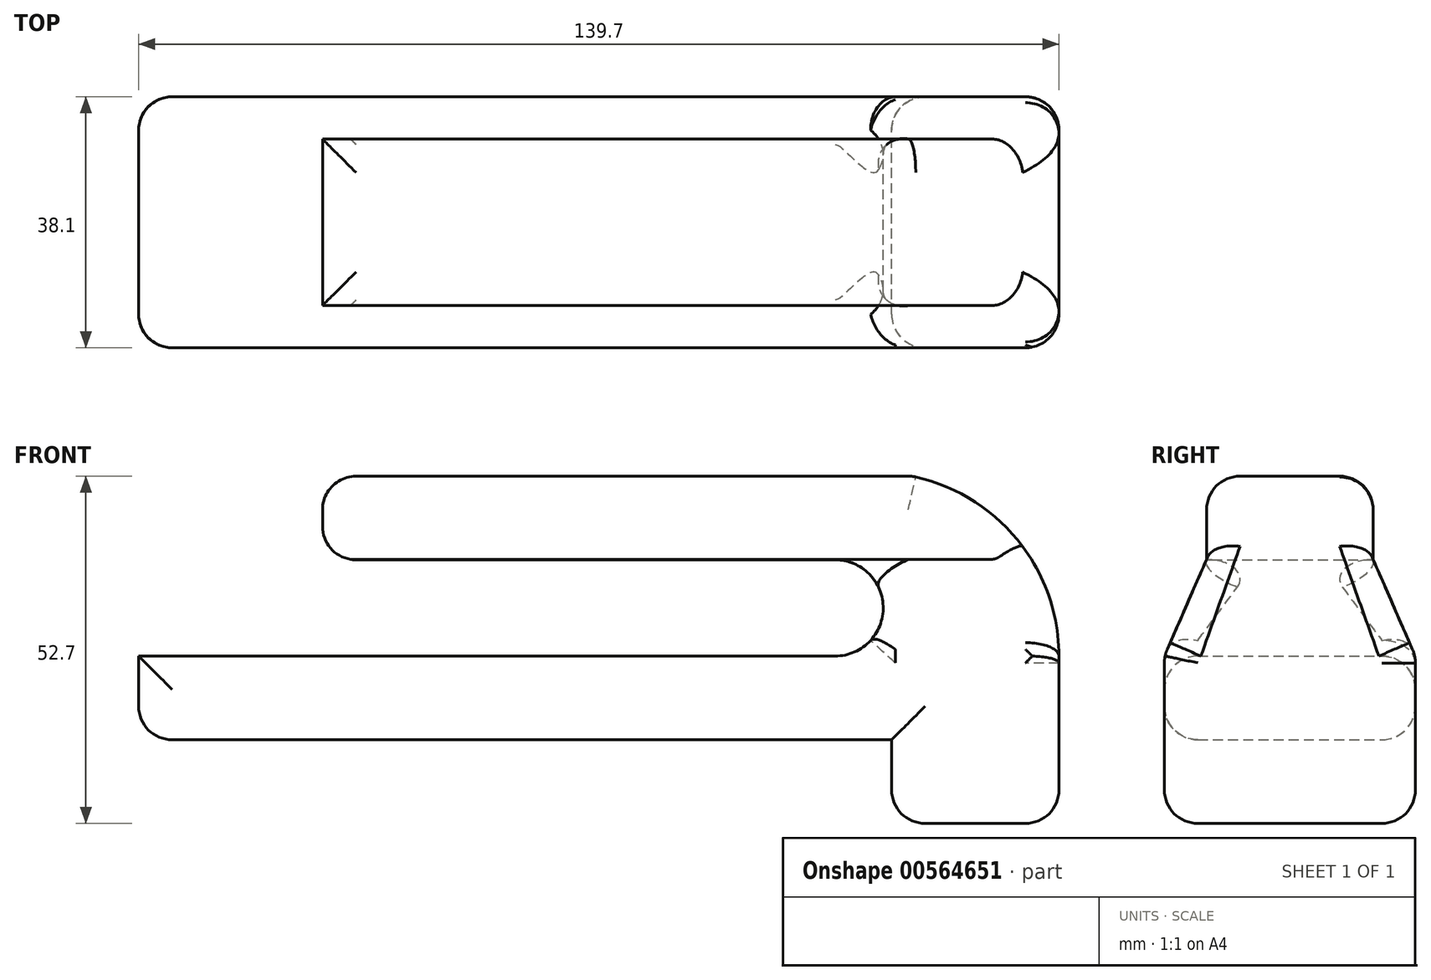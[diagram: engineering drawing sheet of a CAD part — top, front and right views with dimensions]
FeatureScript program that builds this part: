
annotation { "Feature Type Name" : "Feature", "Feature Type Description" : "" }
export const myFeature = defineFeature(function(context is Context, id is Id, definition is map)
    precondition{}
    {
        {
            var Q0;
            Q0=qCreatedBy(makeId("Front.planeOp"),FACE);
            var sketch = newSketch(context, id + "F0", { "sketchPlane" : qUnion([Q0])});
            skLineSegment(sketch, "E0.bottom", {"start": v(67.16, 0) * mm, "end": v(-72.54, 0) * mm});
            skLineSegment(sketch, "E0.left", {"start": v(67.16, 0) * mm, "end": v(67.16, 12.7) * mm});
            skLineSegment(sketch, "E0.right", {"start": v(-72.54, 0) * mm, "end": v(-72.54, 12.7) * mm});
            skLineSegment(sketch, "E1", {"start": v(-44.62, 27.3) * mm, "end": v(-44.62, 40) * mm});
            skLineSegment(sketch, "E2", {"start": v(-44.62, 40) * mm, "end": v(44.84, 40) * mm});
            skArc(sketch, "E3", {"start": v(67.16, 12.7) * mm, "mid": v(60.87, 30.33) * mm, "end": v(44.84, 40) * mm});
            skLineSegment(sketch, "E4", {"start": v(73.54, 0) * mm, "end": v(73.54, 49.57) * mm});
            skLineSegment(sketch, "E5", {"start": v(-44.62, 27.3) * mm, "end": v(33.18, 27.3) * mm});
            skArc(sketch, "E6", {"start": v(33.18, 12.7) * mm, "mid": v(40.48, 20) * mm, "end": v(33.18, 27.3) * mm});
            skLineSegment(sketch, "E7", {"start": v(-72.54, 12.7) * mm, "end": v(33.18, 12.7) * mm});
            skLineSegment(sketch, "E8.bottom", {"start": v(67.16, 0) * mm, "end": v(41.76, 0) * mm});
            skLineSegment(sketch, "E8.top", {"start": v(67.16, -12.7) * mm, "end": v(41.76, -12.7) * mm});
            skLineSegment(sketch, "E8.left", {"start": v(67.16, 0) * mm, "end": v(67.16, -12.7) * mm});
            skLineSegment(sketch, "E8.right", {"start": v(41.76, 0) * mm, "end": v(41.76, -12.7) * mm});
            skSolve(sketch);
        }
        {
            var Q0;
            Q0=qSketchRegion(id+"F0",true);
            extrude(context, id + "F1", {"entities" : qUnion([Q0]), "depth" : 38.1 * mm, "offsetDistance" : 25.4 * mm});
        }
        {
            var Q0;
            Q0=qCreatedBy(makeId("Right.planeOp"),FACE);
            var sketch = newSketch(context, id + "F2", { "sketchPlane" : qUnion([Q0])});
            skLineSegment(sketch, "E9", {"start": v(0, 12.7) * mm, "end": v(0, 40.1) * mm});
            skLineSegment(sketch, "E10", {"start": v(0, 12.7) * mm, "end": v(-6.42, 27.37) * mm});
            skLineSegment(sketch, "E11", {"start": v(-31.69, 27.37) * mm, "end": v(-38.1, 12.7) * mm});
            skLineSegment(sketch, "E12", {"start": v(-31.69, 27.37) * mm, "end": v(-31.69, 45.15) * mm});
            skLineSegment(sketch, "E13", {"start": v(-31.69, 45.15) * mm, "end": v(-38.1, 45.15) * mm});
            skLineSegment(sketch, "E14", {"start": v(-38.1, 45.15) * mm, "end": v(-38.1, 12.7) * mm});
            skLineSegment(sketch, "E15", {"start": v(-6.42, 27.37) * mm, "end": v(-6.42, 45.15) * mm});
            skLineSegment(sketch, "E16", {"start": v(0, 12.7) * mm, "end": v(0, 45.15) * mm});
            skLineSegment(sketch, "E17", {"start": v(0, 45.15) * mm, "end": v(-6.42, 45.15) * mm});
            skSolve(sketch);
        }
        {
            var Q0;
            Q0=qSketchRegion(id+"F2",true);
            extrude(context, id + "F3", {"entities" : qUnion([Q0]), "operationType" : NewBodyOperationType.REMOVE, "oppositeDirection" : true, "depth" : -127 * mm, "offsetDistance" : 25.4 * mm});
        }
        {
            var Q0;
            Q0 = qSketchRegion(id + "F2", true);
            extrude(context, id + "F4", {"entities" : qUnion([Q0]), "operationType" : NewBodyOperationType.REMOVE, "depth" : -76.2 * mm, "offsetDistance" : 25.4 * mm});
        }
        {
            var Q0;
            Q0=makeQuery(id+"F4.boolean.opBoolean","INTERSECT",EDGE,{"derivedFrom":[makeQuery(id+"F1.opExtrude","SWEPT_FACE",FACE,{"disambiguationData":[OSD([sQuery(id+"F0.wireOp",EDGE,"E2")])]}),makeQuery(id+"F4.opExtrude","SWEPT_FACE",FACE,{"disambiguationData":[OSD([sQuery(id+"F2.wireOp",EDGE,"E12")])]})]});
            var Q1;
            Q1=makeQuery(id+"F4.boolean.opBoolean","INTERSECT",EDGE,{"derivedFrom":[makeQuery(id+"F1.opExtrude","SWEPT_FACE",FACE,{"disambiguationData":[OSD([sQuery(id+"F0.wireOp",EDGE,"E5")])]}),makeQuery(id+"F4.opExtrude","SWEPT_FACE",FACE,{"disambiguationData":[OSD([sQuery(id+"F2.wireOp",EDGE,"E11")])]})]});
            var Q2;
            Q2=makeQuery(id+"F3.boolean.opBoolean","INTERSECT",EDGE,{"derivedFrom":[makeQuery(id+"F1.opExtrude","SWEPT_FACE",FACE,{"disambiguationData":[OSD([sQuery(id+"F0.wireOp",EDGE,"E3")])]}),makeQuery(id+"F3.opExtrude","SWEPT_FACE",FACE,{"disambiguationData":[OSD([sQuery(id+"F2.wireOp",EDGE,"E12")])]})]});
            var Q3;
            Q3=makeQuery(id+"F3.boolean.opBoolean","INTERSECT",EDGE,{"derivedFrom":[makeQuery(id+"F1.opExtrude","SWEPT_FACE",FACE,{"disambiguationData":[OSD([sQuery(id+"F0.wireOp",EDGE,"E6")])]}),makeQuery(id+"F3.opExtrude","SWEPT_FACE",FACE,{"disambiguationData":[OSD([sQuery(id+"F2.wireOp",EDGE,"E11")])]})]});
            var Q4;
            {var subQ0=sQuery(id+"F0.wireOp",EDGE,"E7");var subQ1=sQuery(id+"F0.wireOp",EDGE,"E6");Q4=makeQuery(id+"F4.boolean.opBoolean","SPLIT",EDGE,{"disambiguationData":[TD([makeQuery(id+"F1.opExtrude","SWEPT_FACE",FACE,{"disambiguationData":[OSD([subQ1])]})])],"derivedFrom":makeQuery(id+"F1.opExtrude","CAP_EDGE",EDGE,{"disambiguationData":[OSD([subQ0])],"isStart":false})});}
            var Q5;
            {var subQ0=sQuery(id+"F0.wireOp",EDGE,"E7");var subQ1=sQuery(id+"F0.wireOp",EDGE,"E0.right");Q5=makeQuery(id+"F4.boolean.opBoolean","SPLIT",EDGE,{"disambiguationData":[TD([makeQuery(id+"F1.opExtrude","SWEPT_FACE",FACE,{"disambiguationData":[OSD([subQ1])]})])],"derivedFrom":makeQuery(id+"F1.opExtrude","CAP_EDGE",EDGE,{"disambiguationData":[OSD([subQ0])],"isStart":false})});}
            var Q6;
            Q6=makeQuery(id+"F1.opExtrude","CAP_EDGE",EDGE,{"disambiguationData":[OSD([sQuery(id+"F0.wireOp",EDGE,"E0.right")])],"isStart":false});
            var Q7;
            {var subQ0=sQuery(id+"F0.wireOp",EDGE,"E3");var subQ1=sQuery(id+"F0.wireOp",EDGE,"E0.right");var subQ2=sQuery(id+"F0.wireOp",EDGE,"E8.left");var subQ3=sQuery(id+"F0.wireOp",EDGE,"E0.left");var subQ4=sQuery(id+"F0.wireOp",EDGE,"E0.bottom");var subQ5=sQuery(id+"F0.wireOp",EDGE,"E8.top");var subQ6=sQuery(id+"F0.wireOp",EDGE,"E6");var subQ7=sQuery(id+"F0.wireOp",EDGE,"E7");var subQ8=sQuery(id+"F0.wireOp",EDGE,"E8.right");Q7=makeQuery(id+"F3.boolean.opBoolean","SPLIT",FACE,{"disambiguationData":[TD([makeQuery(id+"F1.opExtrude","SWEPT_FACE",FACE,{"disambiguationData":[OSD([subQ4])]})])],"derivedFrom":makeQuery(id+"F1.opExtrude","CAP_FACE",FACE,{"disambiguationData":[OSD([subQ4,subQ3,subQ1,sQuery(id+"F0.wireOp",EDGE,"E1"),sQuery(id+"F0.wireOp",EDGE,"E2"),subQ0,sQuery(id+"F0.wireOp",EDGE,"E5"),subQ6,subQ7,subQ5,subQ2,subQ8])],"isStart":false})});}
            var Q8;
            Q8=makeQuery(id+"F1.opExtrude","CAP_EDGE",EDGE,{"disambiguationData":[OSD([sQuery(id+"F0.wireOp",EDGE,"E8.right")])],"isStart":false});
            var Q9;
            Q9=makeQuery(id+"F1.opExtrude","CAP_EDGE",EDGE,{"disambiguationData":[OSD([sQuery(id+"F0.wireOp",EDGE,"E8.top")])],"isStart":false});
            var Q10;
            Q10=makeQuery(id+"F1.opExtrude","CAP_EDGE",EDGE,{"disambiguationData":[OSD([sQuery(id+"F0.wireOp",EDGE,"E0.left"),sQuery(id+"F0.wireOp",EDGE,"E8.left")])],"isStart":false});
            var Q11;
            Q11=makeQuery(id+"F1.opExtrude","CAP_EDGE",EDGE,{"disambiguationData":[OSD([sQuery(id+"F0.wireOp",EDGE,"E0.bottom")])],"isStart":false});
            var Q12;
            Q12=makeQuery(id+"F1.opExtrude","SWEPT_EDGE",EDGE,{"disambiguationData":[OSD([sQuery(id+"F0.wireOp",EDGE,"E1"),sQuery(id+"F0.wireOp",EDGE,"E2")])]});
            var Q13;
            Q13=makeQuery(id+"F1.opExtrude","SWEPT_EDGE",EDGE,{"disambiguationData":[OSD([sQuery(id+"F0.wireOp",EDGE,"E1"),sQuery(id+"F0.wireOp",EDGE,"E5")])]});
            var Q14;
            Q14=makeQuery(id+"F4.boolean.opBoolean","INTERSECT",EDGE,{"derivedFrom":[makeQuery(id+"F1.opExtrude","SWEPT_FACE",FACE,{"disambiguationData":[OSD([sQuery(id+"F0.wireOp",EDGE,"E2")])]}),makeQuery(id+"F4.opExtrude","SWEPT_FACE",FACE,{"disambiguationData":[OSD([sQuery(id+"F2.wireOp",EDGE,"E15")])]})]});
            var Q15;
            Q15=makeQuery(id+"F1.opExtrude","CAP_EDGE",EDGE,{"disambiguationData":[OSD([sQuery(id+"F0.wireOp",EDGE,"E7")])],"isStart":true});
            var Q16;
            Q16=makeQuery(id+"F1.opExtrude","CAP_EDGE",EDGE,{"disambiguationData":[OSD([sQuery(id+"F0.wireOp",EDGE,"E0.right")])],"isStart":true});
            var Q17;
            Q17=makeQuery(id+"F1.opExtrude","SWEPT_EDGE",EDGE,{"disambiguationData":[OSD([sQuery(id+"F0.wireOp",EDGE,"E0.bottom"),sQuery(id+"F0.wireOp",EDGE,"E0.right")])]});
            var Q18;
            Q18=makeQuery(id+"F1.opExtrude","SWEPT_FACE",FACE,{"disambiguationData":[OSD([sQuery(id+"F0.wireOp",EDGE,"E2")])]});
            var Q19;
            Q19=makeQuery(id+"F1.opExtrude","CAP_EDGE",EDGE,{"disambiguationData":[OSD([sQuery(id+"F0.wireOp",EDGE,"E8.top")])],"isStart":true});
            var Q20;
            Q20=makeQuery(id+"F1.opExtrude","SWEPT_EDGE",EDGE,{"disambiguationData":[OSD([sQuery(id+"F0.wireOp",EDGE,"E8.top"),sQuery(id+"F0.wireOp",EDGE,"E8.left")])]});
            var Q21;
            Q21=makeQuery(id+"F1.opExtrude","CAP_EDGE",EDGE,{"disambiguationData":[OSD([sQuery(id+"F0.wireOp",EDGE,"E0.left"),sQuery(id+"F0.wireOp",EDGE,"E8.left")])],"isStart":true});
            fillet(context, id + "F5", {"entities" : qUnion([Q0, Q1, Q2, Q3, Q4, Q5, Q6, Q7, Q8, Q9, Q10, Q11, Q12, Q13, Q14, Q15, Q16, Q17, Q18, Q19, Q20, Q21]), "radius" : 5.08 * mm, "tangentPropagation" : true, "allowEdgeOverflow" : false});
        }
        {
            var Q0;
            Q0=makeQuery(id+"F3.boolean.opBoolean","INTERSECT",EDGE,{"derivedFrom":[makeQuery(id+"F1.opExtrude","SWEPT_FACE",FACE,{"disambiguationData":[OSD([sQuery(id+"F0.wireOp",EDGE,"E3")])]}),makeQuery(id+"F3.opExtrude","SWEPT_FACE",FACE,{"disambiguationData":[OSD([sQuery(id+"F2.wireOp",EDGE,"E11")])]})]});
            var Q1;
            Q1=makeQuery(id+"F3.boolean.opBoolean","INTERSECT",EDGE,{"derivedFrom":[makeQuery(id+"F1.opExtrude","SWEPT_FACE",FACE,{"disambiguationData":[OSD([sQuery(id+"F0.wireOp",EDGE,"E3")])]}),makeQuery(id+"F3.opExtrude","SWEPT_FACE",FACE,{"disambiguationData":[OSD([sQuery(id+"F2.wireOp",EDGE,"E15")])]})]});
            var Q2;
            Q2=makeQuery(id+"F5.opFillet","BLEND_EDGE",EDGE,{"blendedFrom":[makeQuery(id+"F4.boolean.opBoolean","INTERSECT",EDGE,{"derivedFrom":[makeQuery(id+"F1.opExtrude","SWEPT_FACE",FACE,{"disambiguationData":[OSD([sQuery(id+"F0.wireOp",EDGE,"E2")])]}),makeQuery(id+"F4.opExtrude","SWEPT_FACE",FACE,{"disambiguationData":[OSD([sQuery(id+"F2.wireOp",EDGE,"E15")])]})]}),makeQuery(id+"F1.opExtrude","SWEPT_FACE",FACE,{"disambiguationData":[OSD([sQuery(id+"F0.wireOp",EDGE,"E3")])]})],"blendedInto":[makeQuery(id+"F1.opExtrude","SWEPT_FACE",FACE,{"disambiguationData":[OSD([sQuery(id+"F0.wireOp",EDGE,"E3")])]})]});
            var Q3;
            {var subQ0=sQuery(id+"F2.wireOp",EDGE,"E10");Q3=makeQuery(id+"F5.opFillet","BLEND_EDGE",EDGE,{"blendedFrom":[makeQuery(id+"F1.opExtrude","CAP_EDGE",EDGE,{"disambiguationData":[OSD([sQuery(id+"F0.wireOp",EDGE,"E3")])],"isStart":true}),makeQuery(id+"F4.boolean.opBoolean","MERGE",FACE,{"derivedFrom":[makeQuery(id+"F3.boolean.opBoolean","COPY",FACE,{"derivedFrom":makeQuery(id+"F3.opExtrude","SWEPT_FACE",FACE,{"disambiguationData":[OSD([subQ0])]})}),makeQuery(id+"F4.opExtrude","SWEPT_FACE",FACE,{"disambiguationData":[OSD([subQ0])]})]})],"blendedInto":[makeQuery(id+"F4.boolean.opBoolean","MERGE",FACE,{"derivedFrom":[makeQuery(id+"F3.boolean.opBoolean","COPY",FACE,{"derivedFrom":makeQuery(id+"F3.opExtrude","SWEPT_FACE",FACE,{"disambiguationData":[OSD([subQ0])]})}),makeQuery(id+"F4.opExtrude","SWEPT_FACE",FACE,{"disambiguationData":[OSD([subQ0])]})]})]});}
            var Q4;
            Q4=makeQuery(id+"F1.opExtrude","CAP_EDGE",EDGE,{"disambiguationData":[OSD([sQuery(id+"F0.wireOp",EDGE,"E0.bottom")])],"isStart":true});
            var Q5;
            Q5=makeQuery(id+"F1.opExtrude","CAP_EDGE",EDGE,{"disambiguationData":[OSD([sQuery(id+"F0.wireOp",EDGE,"E8.right")])],"isStart":true});
            var Q6;
            Q6=makeQuery(id+"F4.boolean.opBoolean","INTERSECT",EDGE,{"derivedFrom":[makeQuery(id+"F1.opExtrude","SWEPT_FACE",FACE,{"disambiguationData":[OSD([sQuery(id+"F0.wireOp",EDGE,"E5")])]}),makeQuery(id+"F4.opExtrude","SWEPT_FACE",FACE,{"disambiguationData":[OSD([sQuery(id+"F2.wireOp",EDGE,"E10")])]})]});
            fillet(context, id + "F6", {"entities" : qUnion([Q0, Q1, Q2, Q3, Q4, Q5, Q6]), "radius" : 5.08 * mm, "tangentPropagation" : true, "allowEdgeOverflow" : false});
        }
    });
